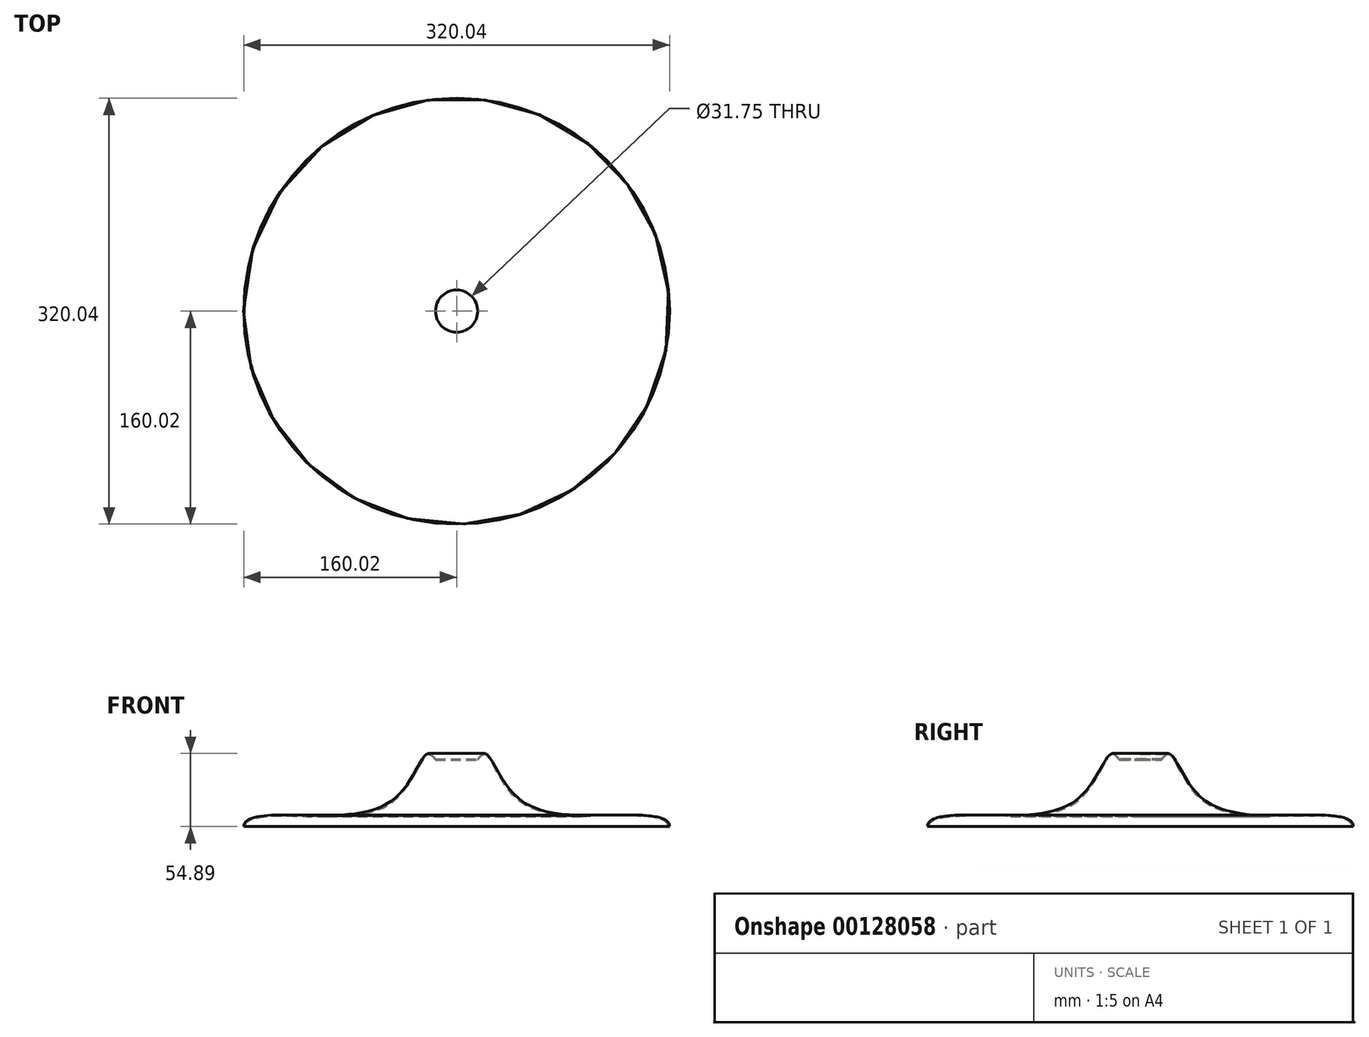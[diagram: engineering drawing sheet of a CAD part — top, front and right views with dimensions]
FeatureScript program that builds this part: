
annotation { "Feature Type Name" : "Feature", "Feature Type Description" : "" }
export const myFeature = defineFeature(function(context is Context, id is Id, definition is map)
    precondition{}
    {
        {
            var Q0;
            Q0=qCreatedBy(makeId("Front.planeOp"),FACE);
            var sketch = newSketch(context, id + "F0", { "sketchPlane" : qUnion([Q0])});
            skLineSegment(sketch, "E0", {"start": v(0, 0) * mm, "end": v(0, 50.04) * mm, "construction": true});
            skLineSegment(sketch, "E1", {"start": v(0, 0) * mm, "end": v(160.02, 0) * mm, "construction": true});
            skLineSegment(sketch, "E2", {"start": v(0, 50.04) * mm, "end": v(15.88, 50.04) * mm, "construction": true});
            skLineSegment(sketch, "E3", {"start": v(0, 50.04) * mm, "end": v(0, 50.83) * mm, "construction": true});
            skLineSegment(sketch, "E4", {"start": v(0, 50.83) * mm, "end": v(15.88, 50.83) * mm, "construction": true});
            skLineSegment(sketch, "E5", {"start": v(15.88, 50.83) * mm, "end": v(15.88, 50.04) * mm});
            skLineSegment(sketch, "E6", {"start": v(160.02, 0) * mm, "end": v(159.23, 0) * mm});
            skFitSpline(sketch, "E7", {"points": [v(159.23, 0) * mm, v(128.8, 7.95) * mm, v(47.72, 18.57) * mm, v(22.33, 53.84) * mm, v(15.88, 50.04) * mm], "startDerivative": vector(-11.45, 85.64) * mm, "endDerivative": vector(-72.45, -90.71) * mm});
            skFitSpline(sketch, "E8", {"points": [v(15.88, 50.83) * mm, v(22.33, 54.54) * mm, v(47.72, 20.23) * mm, v(128.8, 8.78) * mm, v(160.02, 0) * mm], "startDerivative": vector(60.2, 77.5) * mm, "endDerivative": vector(-2.07, -93.26) * mm});
            skSolve(sketch);
        }
        {
            var Q0;
            Q0=makeQuery(id+"F0.imprint","IMPRINT",FACE,{"disambiguationData":[TD([[makeQuery(id+"F0.imprint","IMPRINT",EDGE,{"derivedFrom":sQuery(id+"F0.wireOp",EDGE,"E5")}),1.0]])]});
            var Q1;
            Q1=sQuery(id+"F0.wireOp",EDGE,"E0");
            revolve(context, id + "F1", {"entities" : qUnion([Q0]), "axis" : qUnion([Q1]), "revolveType" : RevolveType.FULL});
        }
    });
